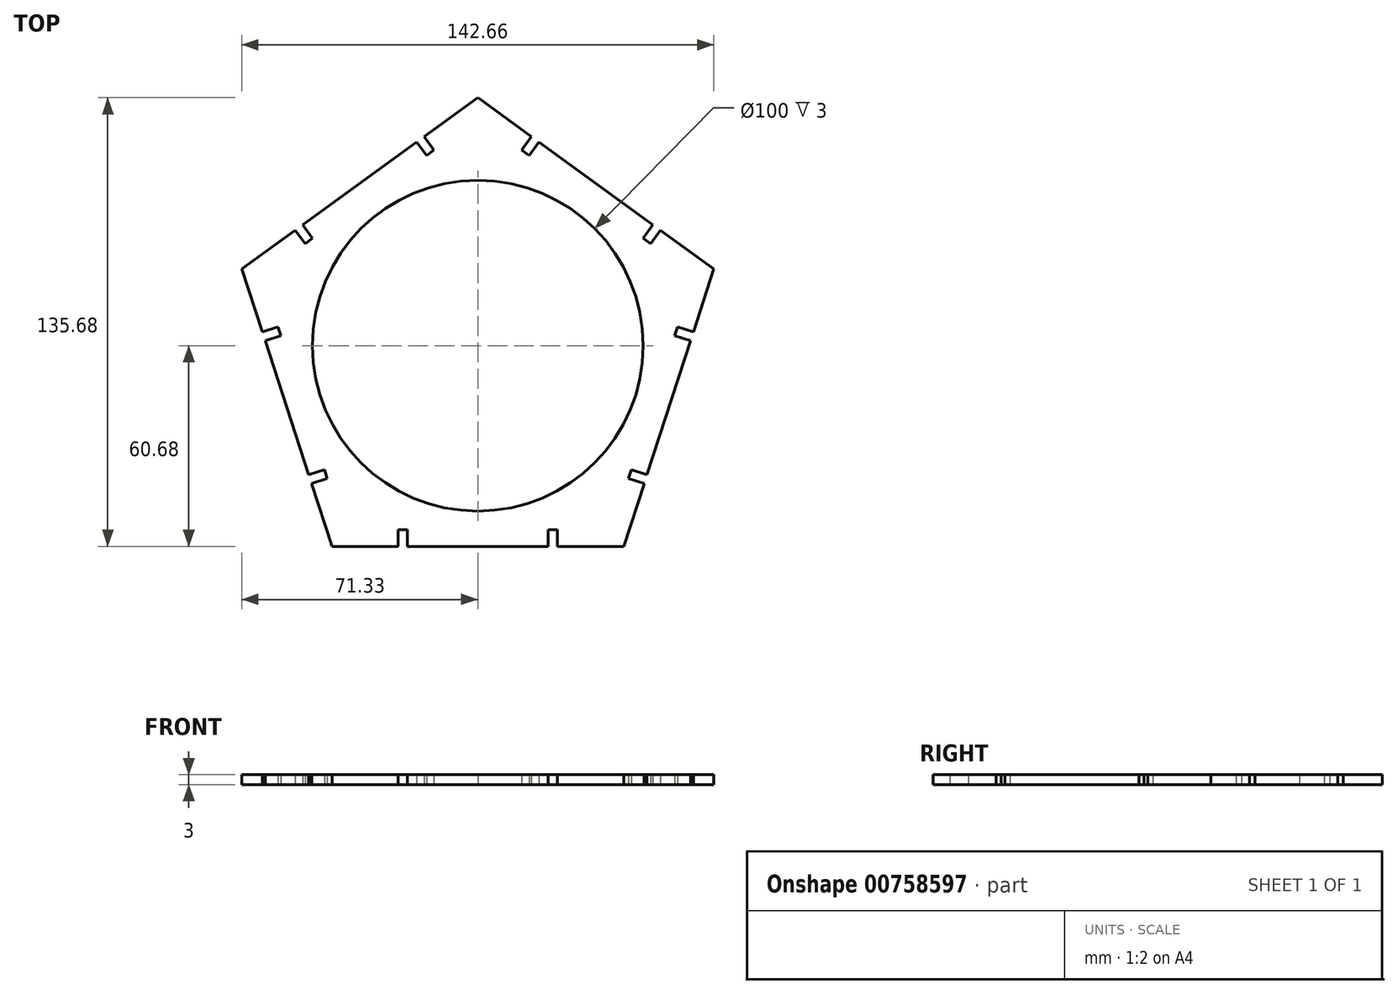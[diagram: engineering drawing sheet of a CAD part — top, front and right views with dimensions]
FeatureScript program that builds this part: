
annotation { "Feature Type Name" : "Feature", "Feature Type Description" : "" }
export const myFeature = defineFeature(function(context is Context, id is Id, definition is map)
    precondition{}
    {
        {
            var Q0;
            Q0=qCreatedBy(makeId("Top.planeOp"),FACE);
            var sketch = newSketch(context, id + "F0", { "sketchPlane" : qUnion([Q0])});
            skCircle(sketch, "E0.cCircle", {"center": v(0, 0) * mm, "radius": 75 * mm, "construction": true});
            skLineSegment(sketch, "E0.0", {"start": v(0, 75) * mm, "end": v(16.18, 63.24) * mm});
            skLineSegment(sketch, "E0.1", {"start": v(71.33, 23.18) * mm, "end": v(65.15, 4.16) * mm});
            skLineSegment(sketch, "E0.2", {"start": v(44.08, -60.68) * mm, "end": v(24.08, -60.68) * mm});
            skLineSegment(sketch, "E0.3", {"start": v(-44.08, -60.68) * mm, "end": v(-50.26, -41.66) * mm});
            skLineSegment(sketch, "E0.4", {"start": v(-71.33, 23.18) * mm, "end": v(-55.15, 34.93) * mm});
            skLineSegment(sketch, "E1", {"start": v(-16.18, 63.24) * mm, "end": v(-13.24, 59.2) * mm});
            skLineSegment(sketch, "E2", {"start": v(-13.24, 59.2) * mm, "end": v(-15.5, 57.55) * mm});
            skLineSegment(sketch, "E3", {"start": v(-15.5, 57.55) * mm, "end": v(-18.45, 61.6) * mm});
            skLineSegment(sketch, "E4", {"start": v(-35.66, 49.09) * mm, "end": v(44.08, -60.68) * mm, "construction": true});
            skLineSegment(sketch, "E5", {"start": v(-44.08, -60.68) * mm, "end": v(35.66, 49.09) * mm, "construction": true});
            skLineSegment(sketch, "E6", {"start": v(-71.33, 23.18) * mm, "end": v(57.7, -18.75) * mm, "construction": true});
            skLineSegment(sketch, "E7", {"start": v(71.33, 23.18) * mm, "end": v(-57.7, -18.75) * mm, "construction": true});
            skLineSegment(sketch, "E8", {"start": v(0, 75) * mm, "end": v(0, -60.68) * mm, "construction": true});
            skLineSegment(sketch, "E9.trimOffspring", {"start": v(-16.18, 63.24) * mm, "end": v(0, 75) * mm});
            skLineSegment(sketch, "E10.MirrorCS", {"start": v(-55.15, 34.93) * mm, "end": v(-52.2, 30.89) * mm});
            skLineSegment(sketch, "E11.MirrorCS", {"start": v(-49.94, 32.53) * mm, "end": v(-52.88, 36.58) * mm});
            skLineSegment(sketch, "E12.MirrorCS", {"start": v(-52.2, 30.89) * mm, "end": v(-49.94, 32.53) * mm});
            skLineSegment(sketch, "E13.trimOffspring", {"start": v(-52.88, 36.58) * mm, "end": v(-18.45, 61.6) * mm});
            skLineSegment(sketch, "E14.1.0", {"start": v(-65.15, 4.16) * mm, "end": v(-60.4, 5.7) * mm});
            skLineSegment(sketch, "E14.1.1", {"start": v(-59.53, 3.04) * mm, "end": v(-64.28, 1.5) * mm});
            skLineSegment(sketch, "E14.1.2", {"start": v(-60.4, 5.7) * mm, "end": v(-59.53, 3.04) * mm});
            skLineSegment(sketch, "E14.1.3", {"start": v(-46.37, -37.45) * mm, "end": v(-51.13, -39) * mm});
            skLineSegment(sketch, "E14.1.4", {"start": v(-45.5, -40.11) * mm, "end": v(-46.37, -37.45) * mm});
            skLineSegment(sketch, "E14.1.5", {"start": v(-50.26, -41.66) * mm, "end": v(-45.5, -40.11) * mm});
            skLineSegment(sketch, "E14.2.0", {"start": v(-24.08, -60.68) * mm, "end": v(-24.08, -55.68) * mm});
            skLineSegment(sketch, "E14.2.1", {"start": v(-21.28, -55.68) * mm, "end": v(-21.28, -60.68) * mm});
            skLineSegment(sketch, "E14.2.2", {"start": v(-24.08, -55.68) * mm, "end": v(-21.28, -55.68) * mm});
            skLineSegment(sketch, "E14.2.3", {"start": v(21.28, -55.68) * mm, "end": v(21.28, -60.68) * mm});
            skLineSegment(sketch, "E14.2.4", {"start": v(24.08, -55.68) * mm, "end": v(21.28, -55.68) * mm});
            skLineSegment(sketch, "E14.2.5", {"start": v(24.08, -60.68) * mm, "end": v(24.08, -55.68) * mm});
            skLineSegment(sketch, "E14.3.0", {"start": v(50.26, -41.66) * mm, "end": v(45.5, -40.11) * mm});
            skLineSegment(sketch, "E14.3.1", {"start": v(46.37, -37.45) * mm, "end": v(51.13, -39) * mm});
            skLineSegment(sketch, "E14.3.2", {"start": v(45.5, -40.11) * mm, "end": v(46.37, -37.45) * mm});
            skLineSegment(sketch, "E14.3.3", {"start": v(59.53, 3.04) * mm, "end": v(64.28, 1.5) * mm});
            skLineSegment(sketch, "E14.3.4", {"start": v(60.4, 5.7) * mm, "end": v(59.53, 3.04) * mm});
            skLineSegment(sketch, "E14.3.5", {"start": v(65.15, 4.16) * mm, "end": v(60.4, 5.7) * mm});
            skLineSegment(sketch, "E14.4.0", {"start": v(55.15, 34.93) * mm, "end": v(52.2, 30.89) * mm});
            skLineSegment(sketch, "E14.4.1", {"start": v(49.94, 32.53) * mm, "end": v(52.88, 36.58) * mm});
            skLineSegment(sketch, "E14.4.2", {"start": v(52.2, 30.89) * mm, "end": v(49.94, 32.53) * mm});
            skLineSegment(sketch, "E14.4.3", {"start": v(15.5, 57.55) * mm, "end": v(18.45, 61.6) * mm});
            skLineSegment(sketch, "E14.4.4", {"start": v(13.24, 59.2) * mm, "end": v(15.5, 57.55) * mm});
            skLineSegment(sketch, "E14.4.5", {"start": v(16.18, 63.24) * mm, "end": v(13.24, 59.2) * mm});
            skLineSegment(sketch, "E15.trimOffspring", {"start": v(-65.15, 4.16) * mm, "end": v(-71.33, 23.18) * mm});
            skLineSegment(sketch, "E16.trimOffspring", {"start": v(21.28, -60.68) * mm, "end": v(-21.28, -60.68) * mm});
            skLineSegment(sketch, "E17.trimOffspring", {"start": v(-24.08, -60.68) * mm, "end": v(-44.08, -60.68) * mm});
            skLineSegment(sketch, "E18.trimOffspring", {"start": v(-51.13, -39) * mm, "end": v(-64.28, 1.5) * mm});
            skLineSegment(sketch, "E19.trimOffspring", {"start": v(18.45, 61.6) * mm, "end": v(52.88, 36.58) * mm});
            skLineSegment(sketch, "E20.trimOffspring", {"start": v(55.15, 34.93) * mm, "end": v(71.33, 23.18) * mm});
            skLineSegment(sketch, "E21.trimOffspring", {"start": v(64.28, 1.5) * mm, "end": v(51.13, -39) * mm});
            skLineSegment(sketch, "E22.trimOffspring", {"start": v(50.26, -41.66) * mm, "end": v(44.08, -60.68) * mm});
            skCircle(sketch, "E23.cCircle", {"center": v(0, 0) * mm, "radius": 50 * mm});
            skPoint(sketch, "E23.0.midPoint", {"position": v(0, 50) * mm});
            skSolve(sketch);
        }
        {
            var Q0;
            Q0=qSketchRegion(id+"F0",true);
            extrude(context, id + "F1", {"entities" : qUnion([Q0]), "depth" : 3 * mm, "offsetDistance" : 25 * mm});
        }
    });
